# Revit family: One Meter
name_source: partatom
category: Lighting Fixtures
units: mm (PartAtom-declared; Revit-internal decimal feet)

## family parameters
Always vertical = Yes
Cut with Voids When Loaded = No
Light Source = Yes
OmniClass Number = 23.80.70.00
OmniClass Title = Lighting
Part Type = Normal
Room Calculation Point = No
Round Connector Dimension = Use Diameter
Shared = No
Work Plane-Based = No

## types (1)
- One Meter
    ArticleNumber = 213413
    AssetType = Movable
    Brand = Pholc
    Cable length = 25cm
    Category = Table lamp
    Class = Class 2
    Color = NCS S 0515-Y
    Color Filter = 16777215
    Default Elevation = 0 mm  [stored 0 ft]
    Dimensions (cm) = 32x32x100
    Dimmable = Yes
    Dimming Lamp Color Temperature Shift = <None>
    IP = IP20
    IP_Code = IP20
    Item no = 213413
    Light Source Symbol Size = 100 mm  [stored 0.328084 ft]
    Lightsource included = Yes
    Lightsource type = Par 20
    Manufacturer = Pholc
    ManufacturerName = Pholc
    ManufacturerURL = https://www.pholc.se
    Material Outer = COCCON
    Max watt = 15 W
    Model = One Meter
    NBSReference = 90-60-50/405
    Nominal Height = 1000 mm  [stored 3.28084 ft]
    Nominal length = 320 mm  [stored 1.04987 ft]
    Nominal width = 320 mm  [stored 1.04987 ft]
    NominalCurrent = 0 A
    NominalVoltage = 0 V
    Rechargeble = No
    Shape = Sculptured
    Size = 32x32x100
    Socket = E27
    TotalWattage = 15 W
    URL = https://www.pholc.se
    Uniclass2 = Pr_70_70_49_43
    Uniclass2015Description = Free standing luminaires
    Uniclass2015Reference = Pr_70_70_48_32
    VisualHusRef = Pholc_Id082

note: [stored X ft] marks values corroborated as IEEE doubles in the binary element streams (Revit-internal decimal feet)

## geometry (parser evidence)
native form markers: Sweep x3
no freeform markers — native parametric forms only
